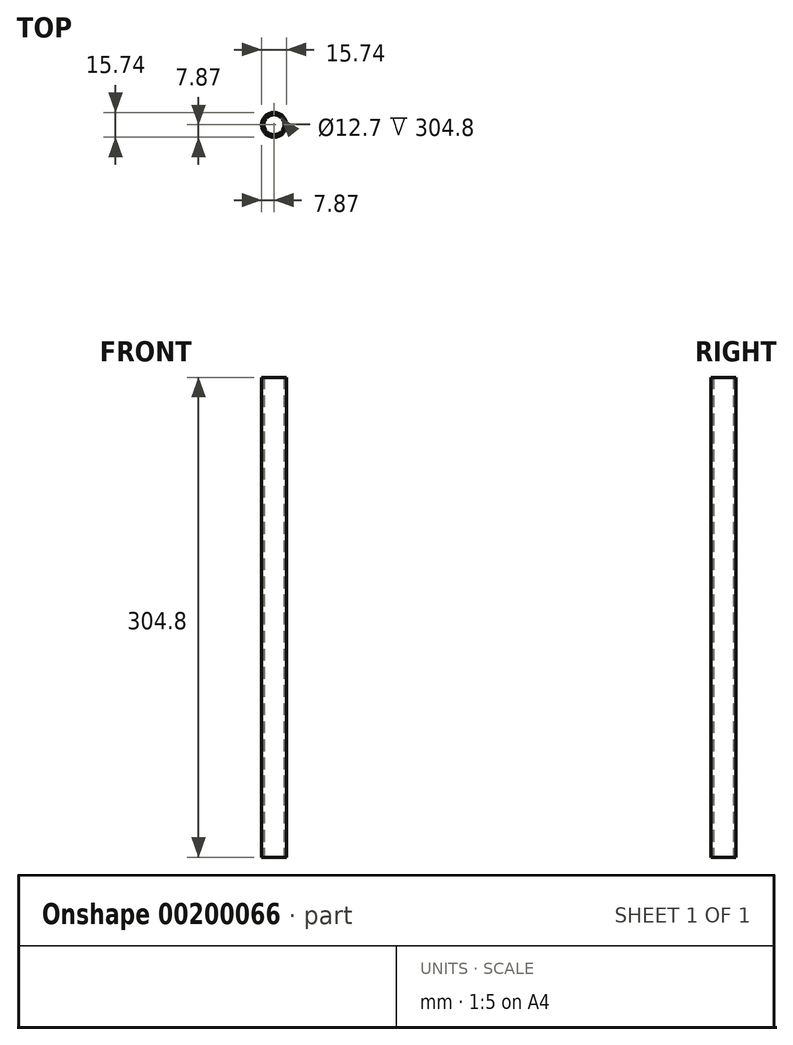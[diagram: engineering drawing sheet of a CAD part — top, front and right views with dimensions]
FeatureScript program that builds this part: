
annotation { "Feature Type Name" : "Feature", "Feature Type Description" : "" }
export const myFeature = defineFeature(function(context is Context, id is Id, definition is map)
    precondition{}
    {
        {
            var Q0;
            Q0=qCreatedBy(makeId("Top.planeOp"),FACE);
            var sketch = newSketch(context, id + "F0", { "sketchPlane" : qUnion([Q0])});
            skCircle(sketch, "E0", {"center": v(0, 0) * mm, "radius": 7.87 * mm});
            skCircle(sketch, "E1.0", {"center": v(0, 0) * mm, "radius": 6.35 * mm});
            skSolve(sketch);
        }
        {
            var Q0;
            Q0=makeQuery(id+"F0.imprint","IMPRINT",FACE,{"disambiguationData":[TD([[makeQuery(id+"F0.imprint","IMPRINT",EDGE,{"derivedFrom":sQuery(id+"F0.wireOp",EDGE,"E0")}),1.0]])]});
            extrude(context, id + "F1", {"entities" : qUnion([Q0]), "depth" : 304.8 * mm});
        }
    });
